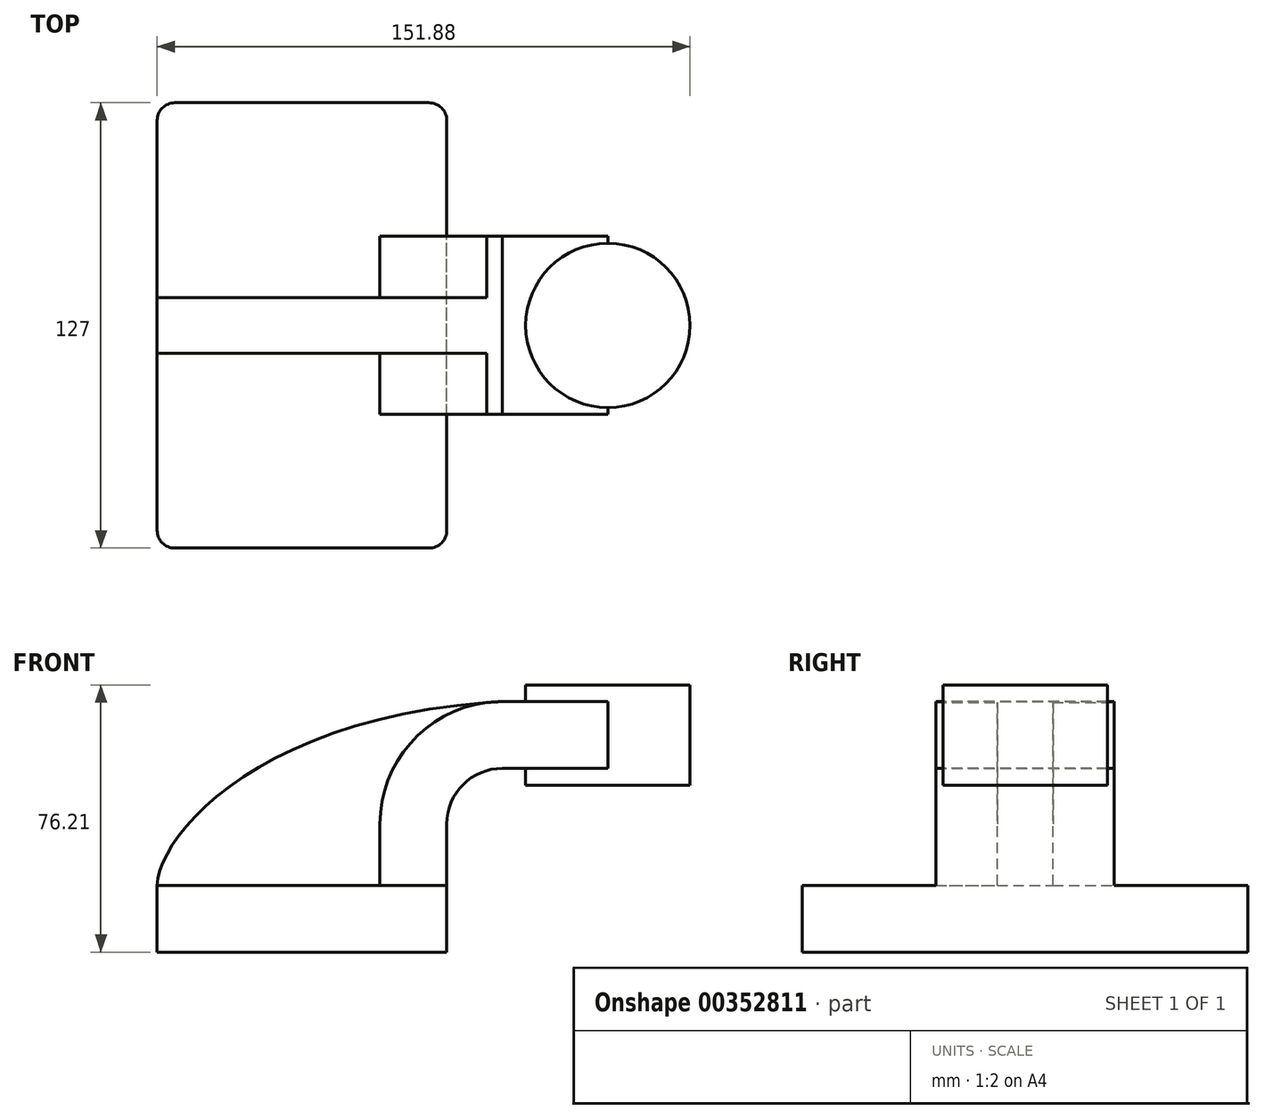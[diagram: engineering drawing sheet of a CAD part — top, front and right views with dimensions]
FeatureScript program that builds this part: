
annotation { "Feature Type Name" : "Feature", "Feature Type Description" : "" }
export const myFeature = defineFeature(function(context is Context, id is Id, definition is map)
    precondition{}
    {
        {
            var Q0;
            Q0=qCreatedBy(makeId("Front.planeOp"),FACE);
            var sketch = newSketch(context, id + "F0", { "sketchPlane" : qUnion([Q0])});
            skLineSegment(sketch, "E0.bottom", {"start": v(-41.28, 9.52) * mm, "end": v(41.28, 9.53) * mm});
            skLineSegment(sketch, "E0.top", {"start": v(-41.28, -9.53) * mm, "end": v(41.28, -9.53) * mm});
            skLineSegment(sketch, "E0.left", {"start": v(-41.28, 9.52) * mm, "end": v(-41.27, -9.53) * mm});
            skLineSegment(sketch, "E0.right", {"start": v(41.28, 9.53) * mm, "end": v(41.28, -9.52) * mm});
            skPoint(sketch, "E0.middle", {"position": v(0, 0) * mm});
            skLineSegment(sketch, "E1.bottom", {"start": v(59.8, 38.1) * mm, "end": v(110.6, 38.1) * mm});
            skLineSegment(sketch, "E1.top", {"start": v(59.8, 66.67) * mm, "end": v(110.6, 66.67) * mm});
            skLineSegment(sketch, "E1.left", {"start": v(59.8, 38.1) * mm, "end": v(59.8, 66.67) * mm});
            skLineSegment(sketch, "E1.right", {"start": v(110.6, 38.1) * mm, "end": v(110.6, 66.67) * mm});
            skLineSegment(sketch, "E2", {"start": v(41.27, 9.53) * mm, "end": v(41.27, 27) * mm});
            skArc(sketch, "E3", {"start": v(41.27, 27) * mm, "mid": v(45.92, 38.23) * mm, "end": v(57.15, 42.88) * mm});
            skLineSegment(sketch, "E4", {"start": v(57.15, 42.88) * mm, "end": v(87.17, 42.88) * mm});
            skLineSegment(sketch, "E5.0", {"start": v(57.15, 61.93) * mm, "end": v(87.17, 61.93) * mm});
            skArc(sketch, "E5.1", {"start": v(22.22, 27) * mm, "mid": v(32.45, 51.7) * mm, "end": v(57.15, 61.93) * mm});
            skLineSegment(sketch, "E5.2", {"start": v(22.22, 9.53) * mm, "end": v(22.22, 27) * mm});
            skLineSegment(sketch, "E6", {"start": v(87.17, 66.67) * mm, "end": v(87.17, 38.1) * mm});
            skPoint(sketch, "E6.endSnap0", {"position": v(85.2, 38.1) * mm});
            skFitSpline(sketch, "E7", {"points": [v(-41.28, 9.52) * mm, v(57.15, 61.93) * mm], "startDerivative": vector(1.73, 43.73) * mm, "endDerivative": vector(206.53, 11.33) * mm});
            skSolve(sketch);
        }
        {
            var Q0;
            Q0=makeQuery(id+"F0.imprint","IMPRINT",FACE,{"disambiguationData":[TD([[makeQuery(id+"F0.imprint","IMPRINT",EDGE,{"derivedFrom":sQuery(id+"F0.wireOp",EDGE,"E0.top")}),1.0]])]});
            extrude(context, id + "F1", {"entities" : qUnion([Q0]), "endBound" : BoundingType.SYMMETRIC, "depth" : 127 * mm});
        }
        {
            var Q0;
            {var subQ0=sQuery(id+"F0.wireOp",EDGE,"E4");var subQ1=sQuery(id+"F0.wireOp",EDGE,"E1.left");var subQ2=makeQuery(id+"F0.imprint","INTERSECT",VERTEX,{"derivedFrom":[subQ1,subQ0]});Q0=makeQuery(id+"F0.imprint","IMPRINT",FACE,{"disambiguationData":[TD([[makeQuery(id+"F0.imprint","IMPRINT",EDGE,{"disambiguationData":[TD([[subQ2,-1.0]])],"derivedFrom":subQ1}),-1.0]])]});}
            var Q1;
            {var subQ1=sQuery(id+"F0.wireOp",EDGE,"E2");Q1=makeQuery(id+"F0.imprint","IMPRINT",FACE,{"disambiguationData":[TD([[makeQuery(id+"F0.imprint","IMPRINT",EDGE,{"derivedFrom":subQ1}),1.0]])]});}
            extrude(context, id + "F2", {"entities" : qUnion([Q0, Q1]), "operationType" : NewBodyOperationType.ADD, "endBound" : BoundingType.SYMMETRIC, "depth" : 50.8 * mm});
        }
        {
            var Q0;
            {var subQ3=sQuery(id+"F0.wireOp",EDGE,"E5.2");Q0=makeQuery(id+"F0.imprint","IMPRINT",FACE,{"disambiguationData":[TD([[makeQuery(id+"F0.imprint","IMPRINT",EDGE,{"derivedFrom":subQ3}),1.0]])]});}
            extrude(context, id + "F3", {"entities" : qUnion([Q0]), "operationType" : NewBodyOperationType.ADD, "endBound" : BoundingType.SYMMETRIC, "depth" : 15.88 * mm});
        }
        {
            var Q0;
            {var subQ4=sQuery(id+"F0.wireOp",EDGE,"E1.right");Q0=makeQuery(id+"F0.imprint","IMPRINT",FACE,{"disambiguationData":[TD([[makeQuery(id+"F0.imprint","IMPRINT",EDGE,{"derivedFrom":subQ4}),1.0]])]});}
            var Q1;
            Q1=sQuery(id+"F0.wireOp",EDGE,"E6");
            revolve(context, id + "F4", {"operationType" : NewBodyOperationType.ADD, "entities" : qUnion([Q0]), "axis" : qUnion([Q1]), "revolveType" : RevolveType.FULL});
        }
        {
            var Q0;
            Q0=makeQuery(id+"F1.opExtrude","CAP_EDGE",EDGE,{"disambiguationData":[OSD([sQuery(id+"F0.wireOp",EDGE,"E0.left")])],"isStart":false});
            var Q1;
            Q1=makeQuery(id+"F1.opExtrude","CAP_EDGE",EDGE,{"disambiguationData":[OSD([sQuery(id+"F0.wireOp",EDGE,"E0.right")])],"isStart":false});
            var Q2;
            Q2=makeQuery(id+"F1.opExtrude","CAP_EDGE",EDGE,{"disambiguationData":[OSD([sQuery(id+"F0.wireOp",EDGE,"E0.right")])],"isStart":true});
            var Q3;
            Q3=makeQuery(id+"F1.opExtrude","CAP_EDGE",EDGE,{"disambiguationData":[OSD([sQuery(id+"F0.wireOp",EDGE,"E0.left")])],"isStart":true});
            fillet(context, id + "F5", {"entities" : qUnion([Q0, Q1, Q2, Q3]), "radius" : 5.08 * mm, "tangentPropagation" : true, "allowEdgeOverflow" : false});
        }
    });
